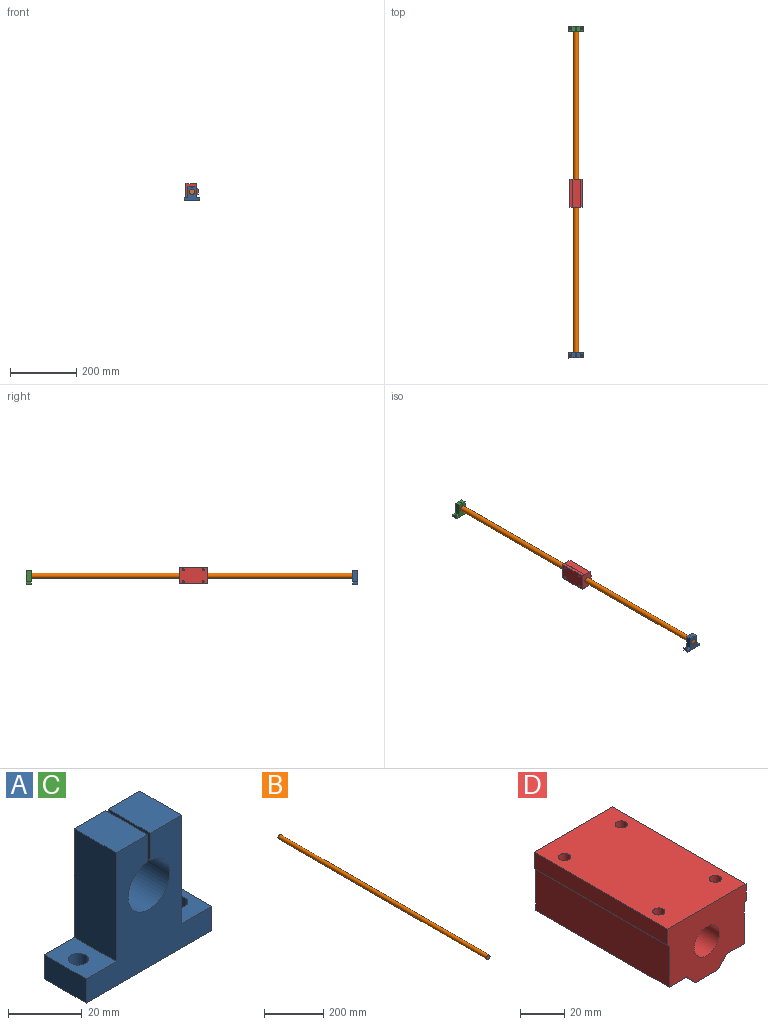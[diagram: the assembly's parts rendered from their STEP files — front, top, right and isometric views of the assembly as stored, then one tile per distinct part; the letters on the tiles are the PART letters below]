
ASSEMBLY  parts=4 mates=3
PART A: 16 faces, bbox 48x16x44 mm
  f0: plane 16x11.5mm, normal (0,0,1), area 160.2mm2, adj f1,f11,f12,f13,f15
  f1: plane 16x8mm, normal (-1,0,0), area 128mm2, adj f0,f2,f12,f13
  f2: plane 48x16mm, normal (0,0,-1), area 720.5mm2, adj f1,f3,f12,f13,f14,f15
  f3: plane 16x8mm, normal (1,0,0), area 128mm2, adj f2,f4,f12,f13
  f4: plane 16x11.5mm, normal (0,0,1), area 160.2mm2, adj f3,f5,f12,f13,f14
  f5: plane 36x16mm, normal (1,0,0), area 576mm2, adj f4,f6,f12,f13
  f6: plane 16x12mm, normal (0,0,1), area 192mm2, adj f5,f7,f12,f13
  f7: plane 16x9.02mm, normal (-1,0,0), area 144.3mm2, adj f6,f8,f12,f13
  f8: cylinder r=8mm len=16mm, axis (0,1,0), area 788.2mm2, adj f7,f9,f12,f13
  f9: plane 16x9.02mm, normal (1,0,0), area 144.3mm2, adj f8,f10,f12,f13
  f10: plane 16x12mm, normal (0,0,1), area 192mm2, adj f9,f11,f12,f13
  f11: plane 36x16mm, normal (-1,0,0), area 576mm2, adj f0,f10,f12,f13
  f12: plane 48x44mm, normal (0,-1,0), area 1073.9mm2, adj f0,f1,f2,f3,f4,f5,f6,f7
  f13: plane 48x44mm, normal (0,1,0), area 1073.9mm2, adj f0,f1,f2,f3,f4,f5,f6,f7
  f14: cylinder r=2.75mm len=8mm, axis (0,0,-1), area 138.2mm2, adj f2,f4
  f15: cylinder r=2.75mm len=8mm, axis (0,0,-1), area 138.2mm2, adj f0,f2
PART B: 3 faces, bbox 16x1000x16 mm
  f0: cylinder r=8mm len=1000mm, axis (0,1,0), area 50265.5mm2, adj f1,f2
  f1: plane 16x16mm, normal (0,-1,0), area 201.1mm2, adj f0
  f2: plane 16x16mm, normal (0,1,0), area 201.1mm2, adj f0
PART C: same geometry as A
PART D: 19 faces, bbox 50x85x38.5 mm
  f0: plane 85x50mm, normal (0,0,1), area 4155mm2, adj f1,f12,f13,f14,f15,f16,f17,f18
  f1: plane 85x9mm, normal (-1,0,0), area 765mm2, adj f0,f2,f13,f14
  f2: plane 85x1mm, normal (-0.68,0,-0.73), area 116.6mm2, adj f1,f3,f13,f14
  f3: plane 85x22.56mm, normal (-1,0,0), area 1917.7mm2, adj f2,f4,f13,f14
  f4: plane 85x11.27mm, normal (0,0,-1), area 910mm2, adj f3,f5,f13,f14,f17,f18
  f5: plane 85x6mm, normal (-0.73,0,-0.68), area 699.6mm2, adj f4,f6,f13,f14
  f6: plane 85x14.2mm, normal (0,0,-1), area 1207.2mm2, adj f5,f7,f13,f14
  f7: plane 85x6mm, normal (0.74,0,-0.68), area 692.8mm2, adj f6,f8,f13,f14
  f8: plane 85x11.38mm, normal (0,0,-1), area 920mm2, adj f7,f9,f13,f14,f15,f16
  f9: plane 85x22.56mm, normal (1,0,0), area 1917.7mm2, adj f8,f10,f13,f14
  f10: plane 85x1mm, normal (0.68,0,-0.73), area 116.6mm2, adj f9,f12,f13,f14
  f11: cylinder r=8mm len=85mm, axis (0,1,0), area 4272.6mm2, adj f13,f14
  f12: plane 85x9mm, normal (1,0,0), area 765mm2, adj f0,f10,f13,f14
  f13: plane 50x38.5mm, normal (0,-1,0), area 1496.5mm2, adj f0,f1,f2,f3,f4,f5,f6,f7
  f14: plane 50x38.5mm, normal (0,1,0), area 1496.5mm2, adj f0,f1,f2,f3,f4,f5,f6,f7
  f15: cylinder r=2.75mm len=32.5mm, axis (0,0,1), area 561.6mm2, adj f0,f8
  f16: cylinder r=2.75mm len=32.5mm, axis (0,0,1), area 561.6mm2, adj f0,f8
  f17: cylinder r=2.75mm len=32.5mm, axis (0,0,1), area 561.6mm2, adj f0,f4
  f18: cylinder r=2.75mm len=32.5mm, axis (0,0,1), area 561.6mm2, adj f0,f4
PLACE A t=(154.84,-540.55,-18.41)mm
PLACE B t=(178.84,443.45,8.59)mm
PLACE C t=(154.84,443.45,-18.41)mm
PLACE D rot(axis=(0,-1,0),90deg) t=(159.84,-17.72,-16.41)mm
MATE cylindrical D.f11 <-> B.f0  axis (0,1,0) through (178.84,-17.72,8.59)mm
MATE fastened C.f8 <-> B.f0  axis (0,1,0) through (178.84,443.45,8.59)mm
MATE fastened A.f8 <-> B.f0  axis (0,-1,0) through (178.84,-556.55,8.59)mm
